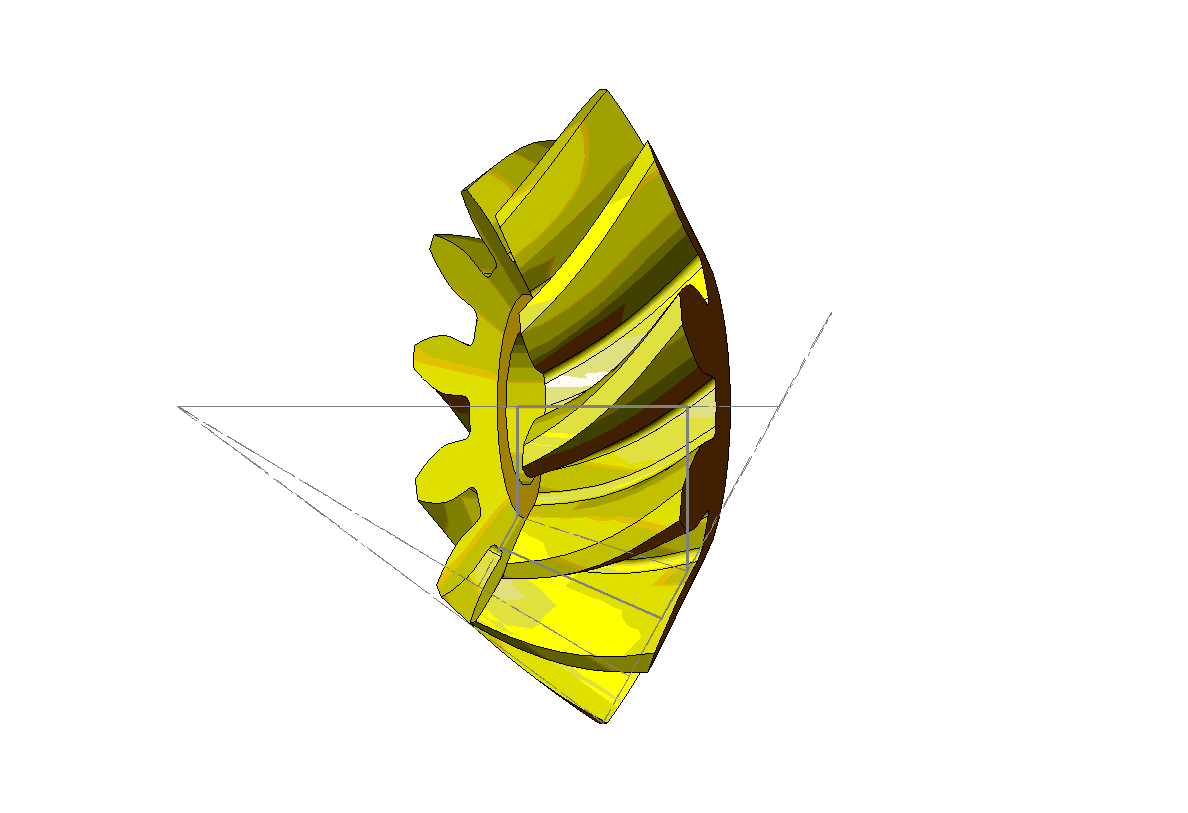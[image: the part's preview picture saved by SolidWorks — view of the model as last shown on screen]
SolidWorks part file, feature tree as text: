
SOLIDWORKS PART (.sldprt)
format: sldprt  version: not decoded by parser v0  size: 2,325,504 bytes
history: native  units: mm
features: sketch x19, plane x9, revolve x2, helix x2, fillet x2, material x1, pattern_circular x1, cut_revolve x1, cut_extrude x1 (+13 scaffold rows collapsed)
feature tree (51):
  scaffold x13  (default folders/planes/origin — collapsed)
  material  "Matériau <non spécifié>"
  plane  "Plan1"
  plane  "Plan2"
  plane  "Plan3"
  sketch  "def"  dims[c1.D1=10.0mm c1.D2=1.0mm c1.D3=1.0mm c1.D4=0.3mm c1.D5=~14.911604mm c2.D1=10.0mm c2.D6=~8.457328mm c2.D2=6.0mm c2.D7=~6.009154mm c2.D3=1.0mm c2.D8=~2.819109mm c2.D4=0.3mm c2.D5=20.0mm c3.D6=1.0mm c3.D7=30.0mm c3.D8=45.0mm]
  sketch  "coneprimitif"  dims[c1.D1=~34.995022mm c2.D1=20.0deg c2.D2=~17.690721mm c2.D3=~34.995022mm c3.D3=~7.287182deg c3.D4=~32.161848mm c4.D4=~4.625522deg c4.D5=30.0mm c4.D1=~29.502859mm c5.D1=30.0deg c5.D2=22.0mm c5.D3=~60.444503mm c6.D3=~11.719591deg c7.D3=~64.323697mm c8.D3=~12.89155deg c8.D4=~64.323697mm c9.D4=~5.729578deg c9.D5=25.0mm c9.D6=~9.645009mm c9.D2=60.0mm c10.D5=20.0mm c10.D6=20.0mm c11.D6=~7.161972deg c11.D7=~6.02008mm c11.D3=7.5mm c11.D4=6.0mm]
  revolve  "conepied"  Angle=360deg
  plane  "Plan complémentaire"
  sketch  "pointdev"  dims[c1.D7=~10.198039mm c1.D8=~10.198039mm c2.D7=18.8mm c2.D9=20.0mm c3.D7=18.8mm c3.D10=~65.103815mm c3.D8=17.5mm c4.D10=17.5mm c4.D1=7.0mm c4.D2=6.0mm c4.D3=1.5mm c4.D4=11.0mm c5.D4=15.0deg c5.D5=11.0mm c6.D5=20.0deg c6.D6=11.0mm c7.D6=25.0deg c7.D1=~11.362759mm c7.D2=~17.044139mm c7.D3=~22.725518mm c7.D4=11.0mm c7.A1=20.0deg c7.D5=11.0mm c7.A2=30.0deg c8.D6=11.0mm c8.A3=40.0deg c8.D8=~15.524175mm c9.D8=4.0deg c10.D8=10.0mm c11.D8=4.0deg c11.D10=10.0mm c12.D10=4.5deg c12.D8=1.0mm c12.D9=1.0mm c13.D8=9.4mm c13.A7=200.0deg c13.D9=~12.133892mm c13.D7=~113.627592mm c13.D10=~10.689046mm c13.D4=~28.406898mm c13.D11=9.4mm c13.A4=50.0deg c13.D12=18.8mm c13.D13=9.8418mm c13.D14=~2.897254mm c13.D32=~2.897254mm c13.D6=~6.888727mm c14.D7=~7.341507mm c14.D8=~7.438531mm c14.D34=~7.438531mm c15.D8=~7.57466mm c15.D6=14.1mm c15.A5=80.0deg c16.D6=~45.451037mm c16.D7=14.1mm c16.A6=120.0deg c17.D7=~68.176555mm c17.D8=~0.832758mm c17.D9=~1.80174mm c17.D11=~3.027617mm c17.D12=~4.387718mm c17.D13=~0.197414mm c17.D14=~0.656143mm c17.D15=~1.522129mm c17.D16=~2.891055mm c17.D17=~1.012442mm c18.D9=1.0mm c18.D13=~1.455907mm c18.D14=1.0mm c18.D15=~4.515206mm c18.D16=~7.676606mm c18.D18=~0.832758mm c18.D19=~1.80174mm c18.D20=~3.004888mm c18.D21=~4.387718mm c18.D22=1.0mm c18.D23=1.0mm c18.D24=1.0mm c18.D25=~1.578211mm c18.D8=~53.401347mm c19.D8=~81.351813deg c19.D9=~17.044139mm c20.D8=~4.515206mm c20.D14=~4.515206mm c20.D5=~45.451037mm c20.D6=~68.176555mm c21.D8=~0.964955mm c21.D17=1.0mm c21.D9=~1.702708mm c21.D18=1.0mm c21.D11=~2.793851mm c21.D19=1.0mm c21.D12=~8.977441mm c21.D20=1.0mm c21.D14=~2.515296mm c22.D18=~3.846345mm c22.D8=~32.551907mm c22.A0=~8.664193deg]
  sketch  "dev"  dims[c1.D7=~10.198039mm c1.D8=~10.198039mm c2.D7=18.8mm c2.D9=20.0mm c3.D7=18.8mm c3.D10=~43.402543mm c3.D8=17.5mm c4.D10=17.5mm c4.D1=7.0mm c4.D2=6.0mm c4.D3=1.5mm c4.D4=11.0mm c5.D4=15.0deg c5.D5=11.0mm c6.D5=20.0deg c6.D6=11.0mm c7.D6=25.0deg c7.D1=~7.575173mm c7.D2=~11.362759mm c7.D3=~15.150346mm c7.D4=11.0mm c7.A1=20.0deg c7.D5=11.0mm c7.A2=30.0deg c8.D6=11.0mm c8.A3=40.0deg c8.D8=~15.524175mm c9.D8=4.0deg c10.D8=10.0mm c11.D8=4.0deg c11.D10=10.0mm c12.D10=4.5deg c12.D8=1.0mm c12.D9=1.0mm c13.D8=9.4mm c13.A5=200.0deg c13.D9=~12.133892mm c13.D5=~75.751728mm c13.D10=~10.689046mm c13.D4=~18.937932mm c13.D11=9.4mm c13.A4=50.0deg c13.D12=18.8mm c13.D13=9.8418mm c13.D14=~2.897254mm c13.D32=~2.897254mm c13.D6=~6.888727mm c13.D7=~7.341507mm c14.D8=~7.438531mm c14.D34=~7.438531mm c15.D8=~7.57466mm c15.D6=14.1mm c15.A6=80.0deg c16.D6=~30.300691mm c16.D7=14.1mm c16.A7=120.0deg c17.D7=~45.451037mm c17.D8=~0.832758mm c17.D9=~1.80174mm c17.D11=~3.027617mm c17.D12=~4.387718mm c17.D13=~0.197414mm c17.D14=~0.656143mm c17.D15=~1.522129mm c17.D16=~2.891055mm c17.D17=1.0mm c18.D13=~1.303938mm c18.D14=~2.010198mm c18.D15=~3.34347mm c18.D16=~5.45107mm c18.D18=~0.832758mm c18.D19=~1.80174mm c18.D20=~3.004888mm c18.D21=~4.387718mm c18.D22=1.0mm c18.D23=1.0mm c18.D24=1.0mm c18.D25=~1.578211mm]
  plane  "Plan radial primitif"
  sketch  "cercle primitif profil départ"
  helix  "héliceconique primitive"  Pitch=17.320508mm
  sketch  "épaisseurdent"  dims[c1.D2=5.0mm c1.D1=~78.016835mm c2.D1=~16.62047deg c2.D2=~8.366764mm]
  plane  "Plan primitif arrivée"
  sketch  "décalageprofilarrivée"  dims[c1.D1=~81.883578mm c2.D1=~9818.417884deg c3.D1=20.0mm c4.D1=~33.079734deg]
  plane  "Plan de section cone profil arrivée"
  sketch  "traces dans ce plan"
  plane  "Plan complémentaire profil arrivée"
  sketch  "pointdev2"  dims[c1.D7=~10.198039mm c1.D8=~10.198039mm c2.D7=18.8mm c2.D9=20.0mm c3.D7=18.8mm c3.D10=~43.402543mm c3.D8=17.5mm c4.D10=17.5mm c4.D1=7.0mm c4.D2=6.0mm c4.D3=1.5mm c4.D4=11.0mm c5.D4=15.0deg c5.D5=11.0mm c6.D5=20.0deg c6.D6=11.0mm c7.D6=25.0deg c7.D1=~3.787586mm c7.D2=~11.362759mm c7.D3=~15.150346mm c7.D4=11.0mm c7.A1=10.0deg c7.D5=11.0mm c7.A2=30.0deg c8.D6=11.0mm c8.A3=40.0deg c8.D8=~15.524175mm c9.D8=4.0deg c10.D8=10.0mm c11.D8=4.0deg c11.D10=10.0mm c12.D10=4.5deg c12.D8=1.0mm c12.D9=1.0mm c13.D8=9.4mm c13.A7=200.0deg c13.D9=~12.133892mm c13.D7=~75.751728mm c13.D10=~10.689046mm c13.D4=~18.937932mm c13.D11=9.4mm c13.A4=50.0deg c13.D12=18.8mm c13.D13=9.8418mm c13.D14=~2.897254mm c13.D32=~2.897254mm c13.D6=~6.888727mm c14.D7=~7.341507mm c14.D8=~7.438531mm c14.D34=~7.438531mm c15.D8=~7.57466mm c15.D6=14.1mm c15.A5=80.0deg c16.D6=~45.451037mm c16.D7=14.1mm c16.A6=120.0deg c17.D7=~68.176555mm c17.D8=~0.832758mm c17.D9=~1.80174mm c17.D11=~3.027617mm c17.D12=~4.387718mm c17.D13=~0.197414mm c17.D14=~0.656143mm c17.D15=~1.522129mm c17.D16=~2.891055mm c17.D17=~1.012442mm c18.D9=1.0mm c18.D13=~0.959778mm c18.D14=1.0mm c18.D15=~1.45839mm c18.D16=~3.669342mm c18.D18=~0.832758mm c18.D19=~1.80174mm c18.D20=~3.004888mm c18.D21=~4.387718mm c18.D22=1.0mm c18.D23=1.0mm c18.D24=1.0mm c18.D25=~1.578211mm c18.D8=~53.401347mm c19.D8=~81.351813deg c19.D9=~17.044139mm c20.D8=~4.515206mm c20.D14=~4.515206mm c20.D5=~30.300691mm c20.D6=~45.451037mm c21.D8=~0.964955mm c21.D17=1.0mm c21.D9=~1.702708mm c21.D18=1.0mm c21.D11=~2.793851mm c21.D19=1.0mm c21.D12=~8.977441mm c21.D20=1.0mm c21.D14=~0.059736mm c22.D18=~3.846345mm c22.D8=~22.765461mm c22.A1=10.0deg c22.D11=~22.765461mm c22.A2=30.0deg c22.D12=~22.765461mm c22.A3=40.0deg c22.D21=~22.765461mm c22.A4=50.0deg c22.D22=~22.765461mm c22.A5=80.0deg c22.D23=~22.765461mm c22.A6=120.0deg c22.D24=~22.765461mm c22.A7=200.0deg c22.sym1=~0.076684mm c22.sym2=~2.020395mm c22.sym3=~4.686941mm c22.sym4=~8.902141mm c22.D16=~1.935278mm c22.D17=~4.509994mm c22.D14=1.0mm c23.D18=~6.634482mm c23.D15=1.0mm c23.D19=~8.142627mm c23.D16=1.0mm c23.D20=~2.124171mm c23.D17=1.0mm c23.D8=~3.565812mm c23.D13=1.0mm c24.D8=~70.868673mm c24.A0=~15.853958deg c25.D8=~22.765461mm c25.A0=~8.664193deg]
  sketch  "dev2"  dims[c1.D7=~10.198039mm c1.D8=~10.198039mm c2.D7=18.8mm c2.D9=20.0mm c3.D7=18.8mm c3.D10=~43.402543mm c3.D8=17.5mm c4.D10=17.5mm c4.D1=7.0mm c4.D2=6.0mm c4.D3=1.5mm c4.D4=11.0mm c5.D4=15.0deg c5.D5=11.0mm c6.D5=20.0deg c6.D6=11.0mm c7.D6=25.0deg c7.D1=~7.575173mm c7.D2=~11.362759mm c7.D3=~15.150346mm c7.D4=11.0mm c7.A1=20.0deg c7.D5=11.0mm c7.A2=30.0deg c8.D6=11.0mm c8.A3=40.0deg c8.D8=~15.524175mm c9.D8=4.0deg c10.D8=10.0mm c11.D8=4.0deg c11.D10=10.0mm c12.D10=4.5deg c12.D8=1.0mm c12.D9=1.0mm c13.D8=9.4mm c13.A5=200.0deg c13.D9=~12.133892mm c13.D5=~75.751728mm c13.D10=~10.689046mm c13.D4=~18.937932mm c13.D11=9.4mm c13.A4=50.0deg c13.D12=18.8mm c13.D13=9.8418mm c13.D14=~2.897254mm c13.D32=~2.897254mm c13.D6=~6.888727mm c13.D7=~7.341507mm c14.D8=~7.438531mm c14.D34=~7.438531mm c15.D8=~7.57466mm c15.D6=14.1mm c15.A6=80.0deg c16.D6=~30.300691mm c16.D7=14.1mm c16.A7=120.0deg c17.D7=~45.451037mm c17.D8=~0.832758mm c17.D9=~1.80174mm c17.D11=~3.027617mm c17.D12=~4.387718mm c17.D13=~0.197414mm c17.D14=~0.656143mm c17.D15=~1.522129mm c17.D16=~2.891055mm c17.D17=1.0mm c18.D13=~1.303938mm c18.D14=~2.010198mm c18.D15=~3.34347mm c18.D16=~5.45107mm c18.D18=~0.832758mm c18.D19=~1.80174mm c18.D20=~3.004888mm c18.D21=~4.387718mm c18.D22=1.0mm c18.D23=1.0mm c18.D24=1.0mm c18.D25=~1.578211mm]
  sketch  "épaisseurdent2"  dims[c1.D2=5.0mm c1.D1=~38.034282mm c2.D1=~16.12047deg c2.D2=~5.57795mm]
  plane  "Plan radial pointe de dent pour hélice"
  sketch  "pointededent"  dims[D1=~74.491661mm D2=~47.778142mm]
  sketch  "angle hélice pointe de dent"  dims[c1.D1=~60.580548mm c2.D1=~37.93848deg c2.D2=~47.778142mm]
  sketch  "cercle de pointe de dent"
  helix  "hélice1"  Pitch=17.320508mm
  sketch  "épaisseurdent copie"  dims[c1.D2=5.0mm c1.D1=~78.016835mm c2.D1=~16.62047deg c2.D2=~8.366764mm]
  sketch  "épaisseurdent2 copie "  dims[c1.D2=5.0mm c1.D1=~38.034282mm c2.D1=~16.12047deg c2.D2=~5.57795mm]
  sketch  "Esquisse9"  dims[D2=0.2mm D3=~20.155644mm D1=0.0mm]
  revolve  "Révolution1"  Angle=360deg
  fillet  "Congé5"  Radius=1mm
  fillet  "Congé6"  Radius=1mm
  pattern_circular  "Répétition circulaire1"  Count=10 Angle=360deg
  sketch  "profil volume révolution longitudinal"  dims[c1.D1=5.0mm c1.D2=1.0mm c1.D3=1.0mm c2.D1=2.0mm c2.D2=~20.099751mm]
  cut_revolve  "rabotage extérieur au cone de tête"  Angle=360deg
  sketch  "alésage"  dims[c1.D1=~41.569219mm c1.D2=44.0mm c2.D1=~3.702643mm c2.D2=2.0mm]
  cut_extrude  "centrage"  [1 undecoded]
decode coverage: 24 of 28 modeling features carry decoded parameters
note: ~ marks probable driven/reference dimensions
note: 1 parameter value undecoded
note: suppression state not decoded; provenance and decode notes live in map.json
